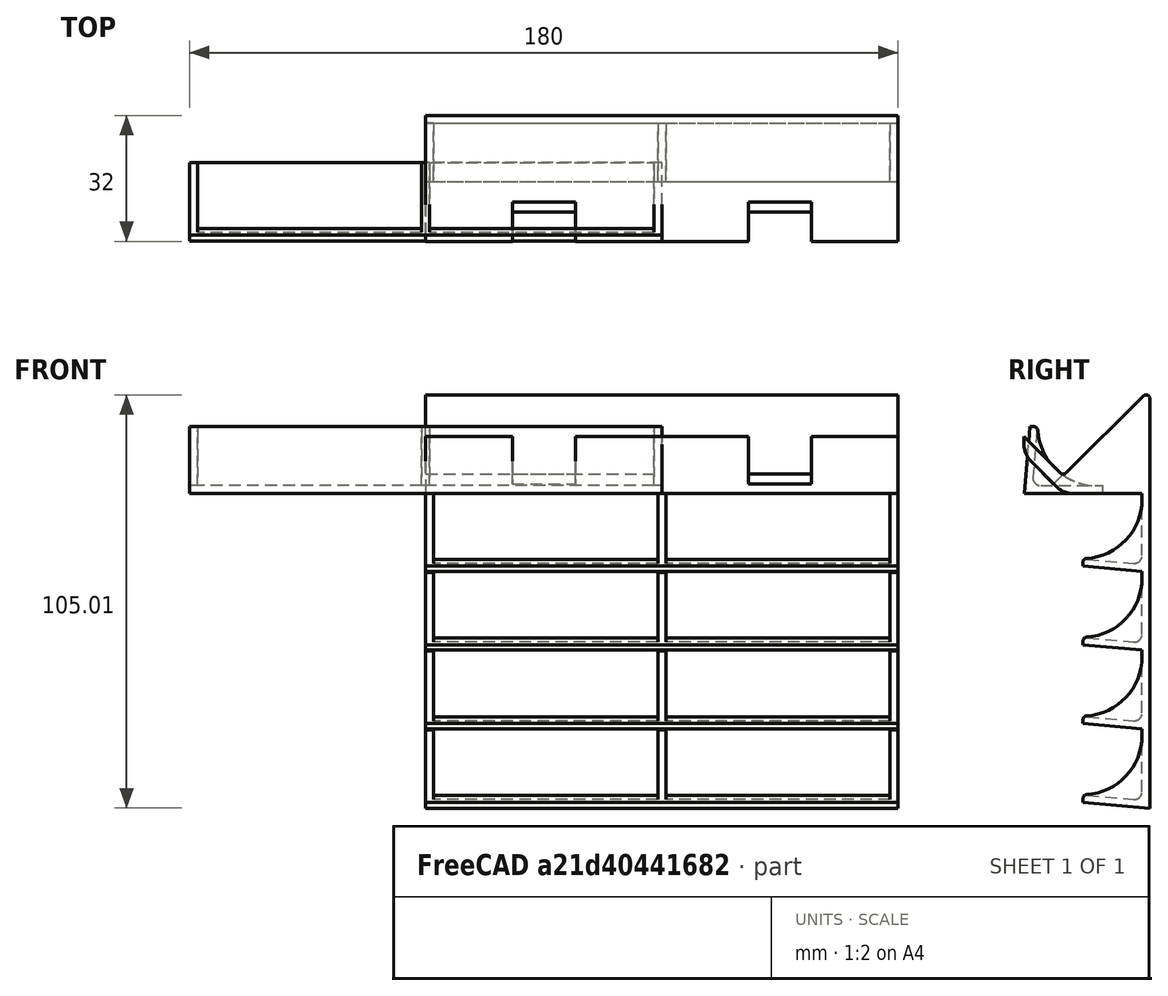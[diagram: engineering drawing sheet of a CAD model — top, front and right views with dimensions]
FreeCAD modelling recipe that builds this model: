
FCSTD DOCUMENT  (FreeCAD 0.20R29177 (Git))
Label: DrzacBrijaca
License: All rights reserved
LicenseURL: http://en.wikipedia.org/wiki/All_rights_reserved
objects: Part::Box×10, Part::Fillet×7, Part::Cut×6, Part::Feature×5, Part::MultiFuse×3, Part::Chamfer×1, Part::Cylinder×1
note: 33 computed .brp shape members not serialized (recipe doc carries the construction recipe); baked Part::Feature solids carry a one-line shape summary decoded from their .brp

FEATURE [Part::Box] Box  label="Cube"
  AttacherType = Attacher::AttachEngine3D
  Height = 27
  Length = 60
  Width = 32
FEATURE [Part::Box] Box001  label="Cube001"
  AttacherType = Attacher::AttachEngine3D
  Height = 32
  Length = 60
  Placement = pos=(0,10,4.5) rot=(1,0,0;0.785398rad)
  Width = 32
FEATURE [Part::Chamfer] Chamfer
  Base = -> Box
  Edges = 1 edges r=10: [Edge9]
FEATURE [Part::Fillet] Fillet002
  Base = -> Chamfer
  Edges = 2 edges r=6: [Edge7,Edge10]
FEATURE [Part::Box] Box003  label="Cube003"
  AttacherType = Attacher::AttachEngine3D
  Height = 16
  Length = 16
  Placement = pos=(22,5,0) rot=(1,0,0;0.785398rad)
  Width = 16
FEATURE [Part::Fillet] Fillet
  Base = -> Box001
  Edges = 1 edges r=1: [Edge9]
FEATURE [Part::Box] Box004  label="Cube004"
  AttacherType = Attacher::AttachEngine3D
  Height = 17
  Length = 20
  Placement = pos=(0,-60,0) rot=(0,0,1;0rad)
  Width = 120
FEATURE [Part::Box] Box005  label="Cube005"
  AttacherType = Attacher::AttachEngine3D
  Height = 25
  Length = 20
  Placement = pos=(-20,-60,0) rot=(0,1,0;0.087266rad)
  Width = 120
FEATURE [Part::Box] Box002  label="Cube002"
  AttacherType = Attacher::AttachEngine3D
  Height = 17
  Length = 20
  Placement = pos=(0,-58.5,0) rot=(0,0,1;0rad)
  Width = 57
FEATURE [Part::Box] Box006  label="Cube006"
  AttacherType = Attacher::AttachEngine3D
  Height = 25
  Length = 20
  Placement = pos=(-20,-60,0) rot=(0,1,0;0.087266rad)
  Width = 120
FEATURE [Part::Cut] Cut002
  Base = -> Box002
  Tool = -> Box006
FEATURE [Part::Cut] Cut003
  Base = -> Box004
  Tool = -> Box005
FEATURE [Part::Cylinder] Cylinder
  Angle = 360
  AttacherType = Attacher::AttachEngine3D
  FirstAngle = 0
  Height = 120
  Placement = pos=(18.5,60,17) rot=(1,0,0;1.5708rad)
  Radius = 15
  SecondAngle = 0
FEATURE [Part::Cut] Cut004
  Base = -> Cut003
  Tool = -> Cylinder
FEATURE [Part::Fillet] Fillet005002  label="Cutout002"
  Base = -> Cut002
  Edges = 1 edges r=2: [Edge7]
  Placement = pos=(2,0.5,2) rot=(0,0,1;0rad)
FEATURE [Part::MultiFuse] Fusion001  label="CutOuts"
  Shapes = -> [Box003,Fillet]
FEATURE [Part::Cut] Cut
  Base = -> Fillet002
  Tool = -> Fusion001
FEATURE [Part::Fillet] Fillet003001002  label="ShaverHolder001"
  Base = -> Cut
  Edges = 1 edges r=1: [Edge21]
FEATURE [Part::Feature] Fillet003001002001  label="ShaverHolder002"
  Placement = pos=(60,0,0) rot=(0,0,1;0rad)
  shape: bbox 60 x 32 x 25.09 mm, 18 faces (baked)
FEATURE [Part::Box] Box007  label="Cube007"
  AttacherType = Attacher::AttachEngine3D
  Height = 17
  Length = 20
  Placement = pos=(0,-58.5,0) rot=(0,0,1;0rad)
  Width = 57
FEATURE [Part::Box] Box008  label="Cube008"
  AttacherType = Attacher::AttachEngine3D
  Height = 25
  Length = 20
  Placement = pos=(-20,-60,0) rot=(0,1,0;0.087266rad)
  Width = 120
FEATURE [Part::Cut] Cut005
  Base = -> Box007
  Tool = -> Box008
FEATURE [Part::Fillet] Fillet003001002002  label="Cutout003"
  Base = -> Cut005
  Edges = 1 edges r=2: [Edge7]
  Placement = pos=(2,59.5,2) rot=(0,0,1;0rad)
FEATURE [Part::MultiFuse] Fusion
  Shapes = -> [Fillet003001002002,Fillet005002]
FEATURE [Part::Cut] Cut006
  Base = -> Cut004
  Tool = -> Fusion
FEATURE [Part::Fillet] Fillet003001002003
  Base = -> Cut006
  Edges = 2 edges r=1: [Edge25,Edge29]
FEATURE [Part::Fillet] Fillet003001002004
  Base = -> Fillet003001002003
  Edges = 3 edges r=1: [Edge5,Edge9,Edge15]
  Placement = pos=(0,0,0) rot=(0,0,1;1.5708rad)
FEATURE [Part::Feature] Fillet003001002004001001001  label="RazorShelf001"
  shape: bbox 120 x 17 x 19.92 mm, 28 faces (baked)
FEATURE [Part::Feature] Fillet003001002004001001002  label="RazorShelf002"
  Placement = pos=(0,0,-20) rot=(0,0,1;0rad)
  shape: bbox 120 x 17 x 19.92 mm, 28 faces (baked)
FEATURE [Part::Feature] Fillet003001002004001001003  label="RazorShelf003"
  Placement = pos=(0,0,-40) rot=(0,0,1;0rad)
  shape: bbox 120 x 17 x 19.92 mm, 28 faces (baked)
FEATURE [Part::Feature] Fillet003001002004001001004  label="RazorShelf004"
  Placement = pos=(0,0,-60) rot=(0,0,1;0rad)
  shape: bbox 120 x 17 x 19.92 mm, 28 faces (baked)
FEATURE [Part::Box] Box009  label="Cube009"
  AttacherType = Attacher::AttachEngine3D
  Height = 100
  Length = 120
  Placement = pos=(0,30,-79) rot=(0,0,1;0rad)
  Width = 2
FEATURE [Part::MultiFuse] Fusion002  label="ShaverHolder"
  Shapes = -> [Box009,Fillet003001002,Fillet003001002001,Fillet003001002004001001001,Fillet003001002004001001002,Fillet003001002004001001003,Fillet003001002004001001004]
